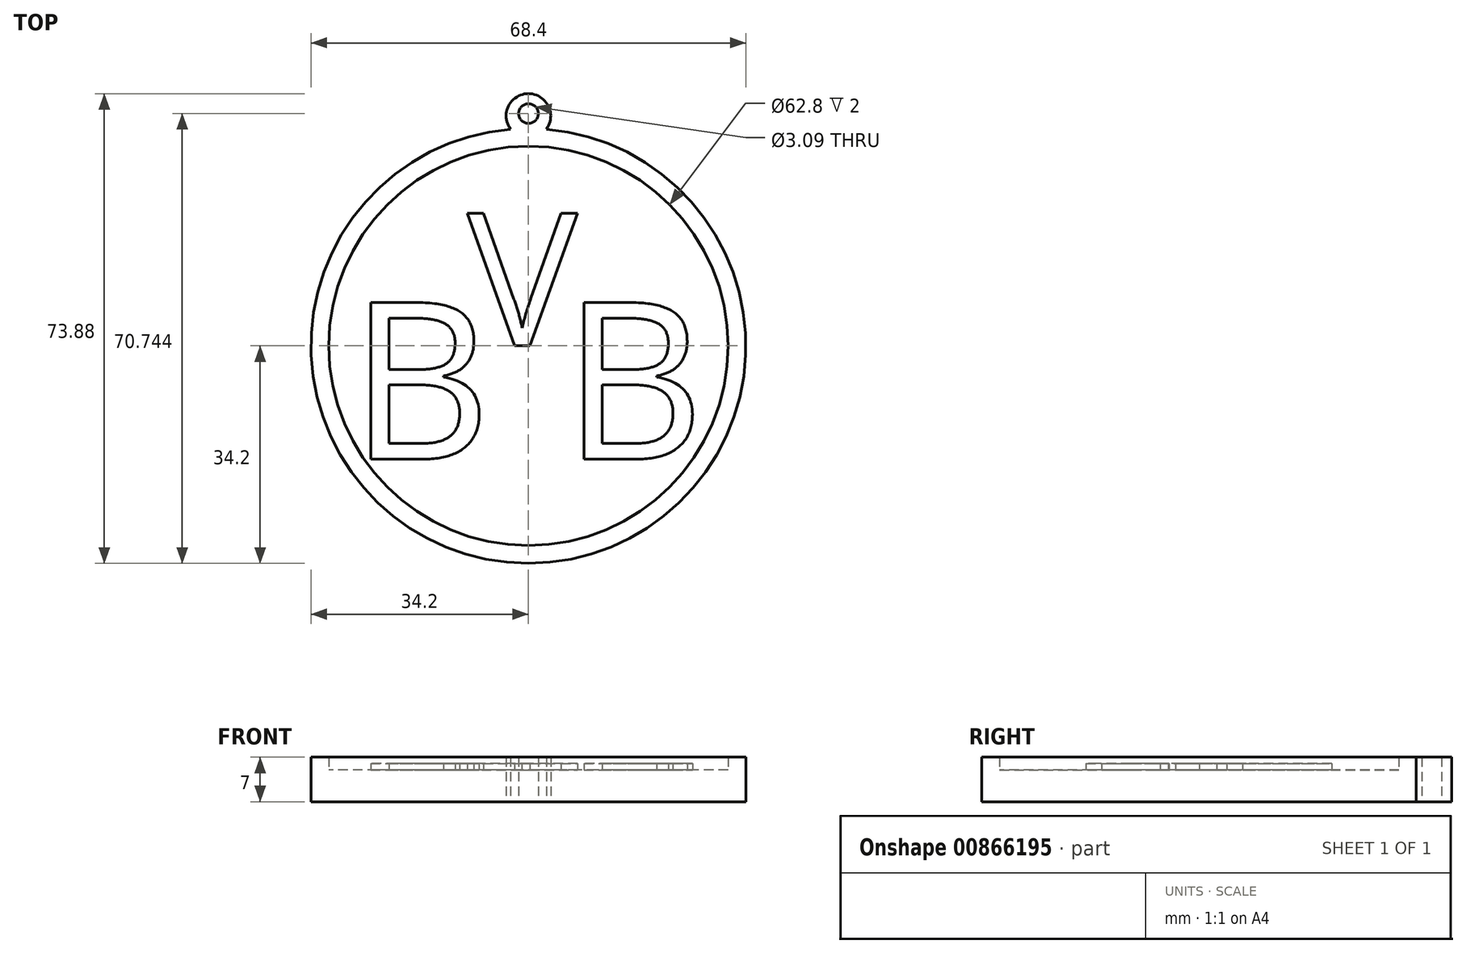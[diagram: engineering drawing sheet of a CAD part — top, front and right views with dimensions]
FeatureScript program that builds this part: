
annotation { "Feature Type Name" : "Feature", "Feature Type Description" : "" }
export const myFeature = defineFeature(function(context is Context, id is Id, definition is map)
    precondition{}
    {
        {
            var Q0;
            Q0=qCreatedBy(makeId("Top.planeOp"),FACE);
            var sketch = newSketch(context, id + "F0", { "sketchPlane" : qUnion([Q0])});
            skCircle(sketch, "E0", {"center": v(0, 0) * mm, "radius": 31.4 * mm});
            skCircle(sketch, "E1", {"center": v(0, 0) * mm, "radius": 34.2 * mm});
            skArc(sketch, "E2", {"start": v(2.81, 34.08) * mm, "mid": v(0, 39.68) * mm, "end": v(-2.81, 34.08) * mm});
            skSolve(sketch);
        }
        {
            var Q0;
            Q0 = qSketchRegion(id + "F0", true);
            extrude(context, id + "F1", {"entities" : qUnion([Q0]), "depth" : 7 * mm, "offsetDistance" : 25 * mm});
        }
        {
            var Q0;
            Q0=makeQuery(id+"F0.imprint","IMPRINT",FACE,{"disambiguationData":[TD([[makeQuery(id+"F0.imprint","IMPRINT",EDGE,{"derivedFrom":sQuery(id+"F0.wireOp",EDGE,"E0")}),1.0]])]});
            extrude(context, id + "F2", {"entities" : qUnion([Q0]), "operationType" : NewBodyOperationType.ADD, "depth" : 5 * mm, "offsetDistance" : 25 * mm});
        }
        {
            var Q0;
            Q0=qCreatedBy(makeId("Top.planeOp"),FACE);
            var sketch = newSketch(context, id + "F3", { "sketchPlane" : qUnion([Q0])});
            skText(sketch, "E3", { "text": "B", "fontName": "OpenSans-Regular.ttf"});
            skText(sketch, "E4", { "text": "B", "fontName": "OpenSans-Regular.ttf"});
            skText(sketch, "E5", { "text": "V", "fontName": "OpenSans-Regular.ttf"});
            const initialGuessF3  = {"E3": [-0.0282, -0.0178, 1, 0, 0.02484], "E4": [0.00534, -0.0178, 1, 0, 0.02484], "E5": [-0.00964, 0, 1, 0, 0.02102]};
            skSetInitialGuess(sketch, initialGuessF3);
            skSolve(sketch);
        }
        {
            var Q0;
            Q0 = qSketchRegion(id + "F3", true);
            extrude(context, id + "F4", {"entities" : qUnion([Q0]), "operationType" : NewBodyOperationType.ADD, "depth" : 6 * mm, "offsetDistance" : 25 * mm});
        }
        {
            var Q0;
            Q0=qCreatedBy(makeId("Top.planeOp"),FACE);
            var sketch = newSketch(context, id + "F5", { "sketchPlane" : qUnion([Q0])});
            skCircle(sketch, "E6", {"center": v(0, 36.54) * mm, "radius": 1.54 * mm});
            skSolve(sketch);
        }
        {
            var Q0;
            Q0 = qSketchRegion(id + "F5", true);
            extrude(context, id + "F6", {"entities" : qUnion([Q0]), "operationType" : NewBodyOperationType.REMOVE, "depth" : 20.6 * mm, "offsetDistance" : 25 * mm});
        }
    });
